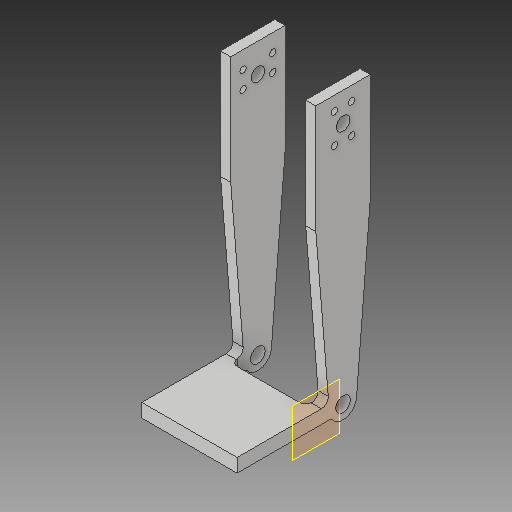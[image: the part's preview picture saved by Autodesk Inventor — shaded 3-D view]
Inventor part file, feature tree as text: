
AUTODESK INVENTOR PART (.ipt)
format: ipt  version: 2019 (Build 230136000, 136)  size: 241,664 bytes
history: native  units: in
note: dims shown in document units (in); Inventor stores cm internally (conversion verified against a paired STEP export)
features: sketch x9, projected_geometry x9, hole x5, extrude x4, plane x2, fillet x2
ambient origin geometry x8: Origin, YZ Plane, XZ Plane, XY Plane, X Axis, Y Axis, Z Axis, Center Point
bodies: Solid1 (feature_tree)
feature tree (31):
  sketch  "Sketch1"  dims[d0=5.0in d1=1.0in]
  plane  "Work Plane1"
  extrude  "Extrusion2"  Depth=1.0in
  plane  "Work Plane2"
  extrude  "Extrusion3"  Depth=0.5in
  hole  "Hole2"  [1 undecoded]
  extrude  "Extrusion4"  Depth=0.5in
  extrude  "Extrusion5"  Depth=1.753in
  fillet  "Fillet1"  Radius=2.0in
  fillet  "Fillet2"  Radius=1.753in
  hole  "Hole3"  [1 undecoded]
  hole  "Hole4"  [1 undecoded]
  hole  "Hole5"  [1 undecoded]
  hole  "Hole6"  [1 undecoded]
  sketch  "Sketch2"  dims[d5=1.0in d6=0.5in]
  projected_geometry  "Projected Loop1"
  sketch  "Sketch4"  dims[d7=0.5in d8=0.0in]
  projected_geometry  "Projected Loop3"
  sketch  "Sketch5"  dims[d9=1.753in d10=0.0in d18=0.5in]
  projected_geometry  "Projected Loop4"
  sketch  "Sketch8"  dims[d19=0.25in d20=2.0in d21=2.0in d22=1.753in d23=0.0in]
  projected_geometry  "Projected Loop9"
  projected_geometry  "Projected Loop10"
  sketch  "Sketch9"  dims[d24=0.27in d25=0.75in d26=0.375in d27=0.25in d28=0.5635in d29=1.0in d30=0.8108in d31=1.75in]
  projected_geometry  "Projected Loop11"
  sketch  "Sketch10"  dims[d32=0.25in d35=5.0in]
  projected_geometry  "Projected Loop12"
  sketch  "Sketch11"  dims[d36=4.875in d37=1.753in d38=0.0in]
  projected_geometry  "Projected Loop13"
  sketch  "Sketch12"  dims[d41=1.753in d42=5.375in d43=1.378in d44=0.1875in d45=5.875in d46=1.0in d47=0.0in d48=0.125in d49=0.125in d50=0.6299in d51=1.0in d52=0.5in d53=0.315in d54=0.1575in d55=0.117in d56=0.75in d57=0.375in d58=0.25in d59=0.5635in d60=1.0in d61=0.8108in d62=0.6299in d63=1.0in d64=0.5in d65=0.315in d66=0.1575in d67=0.117in d68=0.75in d69=0.375in d70=0.25in d71=0.5635in d72=1.0in d73=0.8108in d74=0.32in d75=1.753in d77=0.5in d78=0.75in d79=0.375in d80=0.25in d81=0.5635in d82=0.125in d83=0.0in d84=1.0in d85=0.5in d86=0.5455in d87=0.2728in d88=0.25in d89=0.75in d90=0.375in d91=0.25in d92=0.5635in d93=1.0in d94=0.8108in d95=0.27in d96=0.1975in d97=0.375in]
  projected_geometry  "Projected Loop14"
note: 5 required parameter values undecoded (feature->parameter linkage not recoverable at this tier; creation-order binding heuristic only, values carry confidence <= 0.55)
